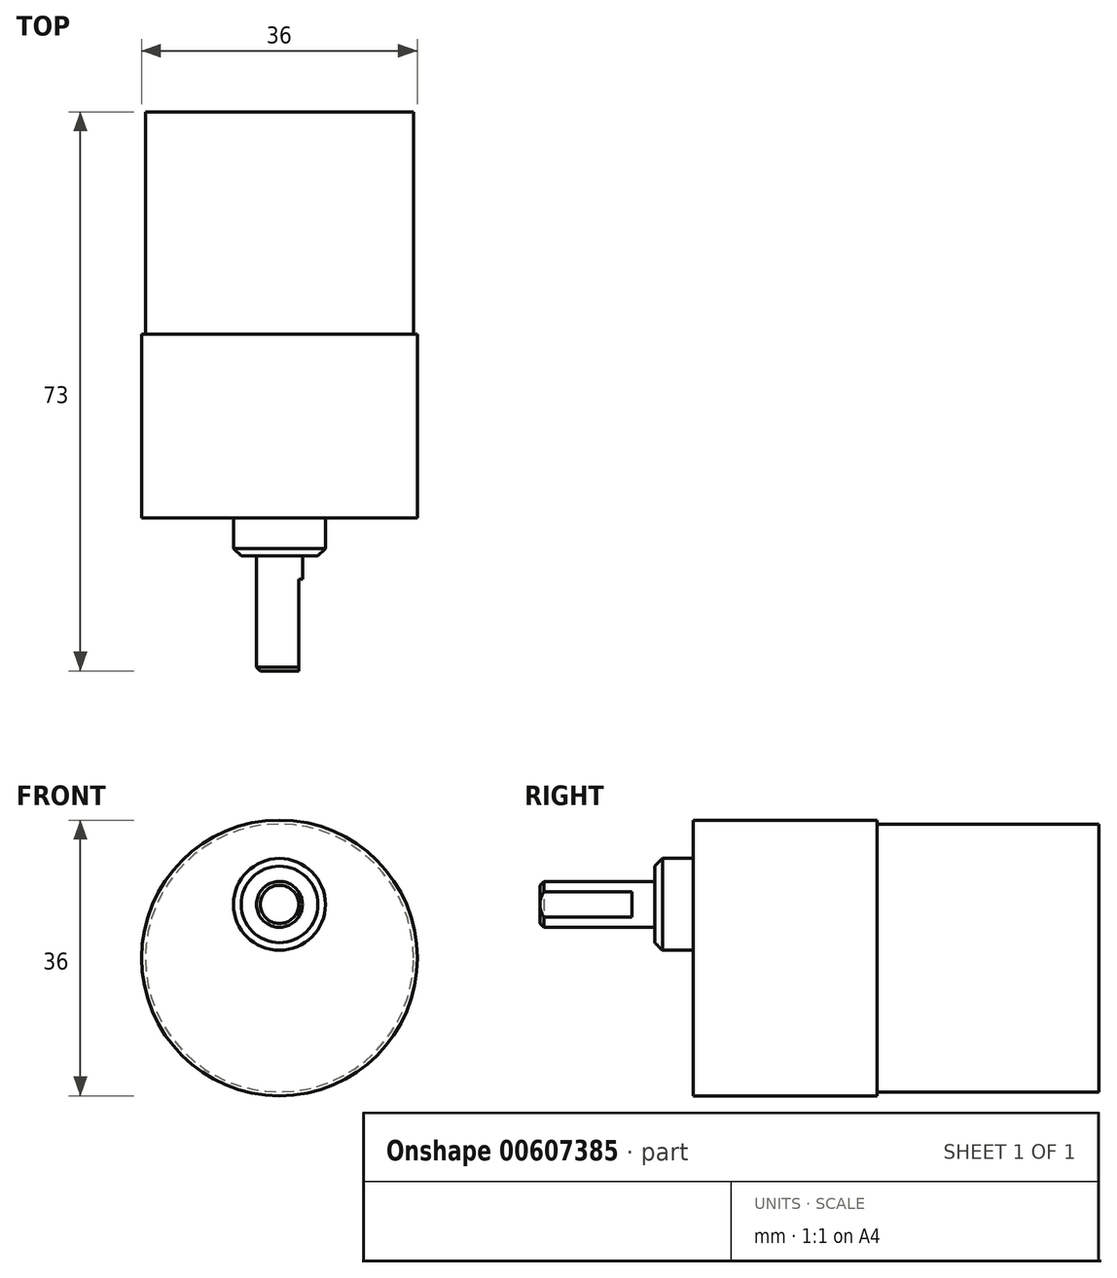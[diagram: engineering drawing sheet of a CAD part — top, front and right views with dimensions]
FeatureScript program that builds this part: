
annotation { "Feature Type Name" : "Feature", "Feature Type Description" : "" }
export const myFeature = defineFeature(function(context is Context, id is Id, definition is map)
    precondition{}
    {
        {
            var Q0;
            Q0=qCreatedBy(makeId("Front.planeOp"),FACE);
            var sketch = newSketch(context, id + "F0", { "sketchPlane" : qUnion([Q0])});
            skCircle(sketch, "E0", {"center": v(0, 0) * mm, "radius": 18 * mm});
            skCircle(sketch, "E1.cCircle", {"center": v(0, 0) * mm, "radius": 18 * mm, "construction": true});
            skLineSegment(sketch, "E1.0", {"start": v(0, -18) * mm, "end": v(-15.59, 9) * mm, "construction": true});
            skLineSegment(sketch, "E1.1", {"start": v(-15.59, 9) * mm, "end": v(15.59, 9) * mm, "construction": true});
            skLineSegment(sketch, "E1.2", {"start": v(15.59, 9) * mm, "end": v(0, -18) * mm, "construction": true});
            skSolve(sketch);
        }
        {
            var Q0;
            Q0 = qSketchRegion(id + "F0", true);
            extrude(context, id + "F1", {"entities" : qUnion([Q0]), "depth" : 24 * mm, "offsetDistance" : 25 * mm});
        }
        {
            var Q0;
            Q0=makeQuery(id+"F1.opExtrude","CAP_FACE",FACE,{"disambiguationData":[OSD([sQuery(id+"F0.wireOp",EDGE,"E0")])],"isStart":false});
            var sketch = newSketch(context, id + "F2", { "sketchPlane" : qUnion([Q0])});
            skCircle(sketch, "E2", {"center": v(0, 7) * mm, "radius": 6 * mm});
            skSolve(sketch);
        }
        {
            var Q0;
            Q0=makeQuery(id+"F2.imprint","IMPRINT",FACE,{"disambiguationData":[TD([[makeQuery(id+"F2.imprint","IMPRINT",EDGE,{"derivedFrom":sQuery(id+"F2.wireOp",EDGE,"E2")}),1.0]])]});
            extrude(context, id + "F3", {"entities" : qUnion([Q0]), "operationType" : NewBodyOperationType.ADD, "depth" : 5 * mm, "offsetDistance" : 25 * mm});
        }
        {
            var Q0;
            Q0=makeQuery(id+"F3.opExtrude","CAP_EDGE",EDGE,{"disambiguationData":[OSD([sQuery(id+"F2.wireOp",EDGE,"E2")])],"isStart":false});
            chamfer(context, id + "F4", {"entities" : qUnion([Q0]), "width" : 1 * mm, "tangentPropagation" : true});
        }
        {
            var Q0;
            Q0=makeQuery(id+"F3.opExtrude","CAP_FACE",FACE,{"disambiguationData":[OSD([sQuery(id+"F2.wireOp",EDGE,"E2")])],"isStart":false});
            var sketch = newSketch(context, id + "F5", { "sketchPlane" : qUnion([Q0])});
            skCircle(sketch, "E3", {"center": v(0, 7) * mm, "radius": 3 * mm});
            skLineSegment(sketch, "E4", {"start": v(2, 9.24) * mm, "end": v(2, 4.76) * mm, "construction": true});
            skSolve(sketch);
        }
        {
            var Q0;
            Q0=makeQuery(id+"F5.imprint","IMPRINT",FACE,{"disambiguationData":[TD([[makeQuery(id+"F5.imprint","IMPRINT",EDGE,{"derivedFrom":sQuery(id+"F5.wireOp",EDGE,"E3")}),1.0]])]});
            var Q1;
            Q1=sQuery(id+"F5.wireOp",EDGE,"E3");
            extrude(context, id + "F6", {"entities" : qUnion([Q0]), "surfaceEntities" : qUnion([Q1]), "depth" : 15 * mm, "offsetDistance" : 25 * mm});
        }
        {
            var Q0;
            Q0=makeQuery(id+"F6.opExtrude","CAP_EDGE",EDGE,{"disambiguationData":[OSD([sQuery(id+"F5.wireOp",EDGE,"E3")])],"isStart":false});
            chamfer(context, id + "F7", {"entities" : qUnion([Q0]), "width" : 0.5 * mm, "tangentPropagation" : true});
        }
        {
            var Q0;
            Q0=makeQuery(id+"F6.opExtrude","CAP_FACE",FACE,{"disambiguationData":[OSD([sQuery(id+"F5.wireOp",EDGE,"E3")])],"isStart":false});
            var sketch = newSketch(context, id + "F8", { "sketchPlane" : qUnion([Q0])});
            skLineSegment(sketch, "E5.bottom", {"start": v(4.5, 9.37) * mm, "end": v(2.5, 9.37) * mm});
            skLineSegment(sketch, "E5.top", {"start": v(4.5, 4.57) * mm, "end": v(2.5, 4.57) * mm});
            skLineSegment(sketch, "E5.left", {"start": v(4.5, 9.37) * mm, "end": v(4.5, 4.57) * mm});
            skLineSegment(sketch, "E5.right", {"start": v(2.5, 9.37) * mm, "end": v(2.5, 4.57) * mm});
            skLineSegment(sketch, "E6", {"start": v(0, 7) * mm, "end": v(4.5, 7) * mm, "construction": true});
            skSolve(sketch);
        }
        {
            var Q0;
            Q0 = qSketchRegion(id + "F8", true);
            extrude(context, id + "F9", {"entities" : qUnion([Q0]), "operationType" : NewBodyOperationType.REMOVE, "oppositeDirection" : true, "depth" : 12 * mm, "offsetDistance" : 25 * mm});
        }
        {
            var Q0;
            Q0=makeQuery(id+"F1.opExtrude","CAP_FACE",FACE,{"disambiguationData":[OSD([sQuery(id+"F0.wireOp",EDGE,"E0")])],"isStart":true});
            var sketch = newSketch(context, id + "F10", { "sketchPlane" : qUnion([Q0])});
            skCircle(sketch, "E7", {"center": v(0, 0) * mm, "radius": 17.5 * mm});
            skSolve(sketch);
        }
        {
            var Q0;
            Q0=makeQuery(id+"F10.imprint","IMPRINT",FACE,{"disambiguationData":[TD([[makeQuery(id+"F10.imprint","IMPRINT",EDGE,{"derivedFrom":sQuery(id+"F10.wireOp",EDGE,"E7")}),1.0]])]});
            extrude(context, id + "F11", {"entities" : qUnion([Q0]), "operationType" : NewBodyOperationType.ADD, "depth" : 29 * mm, "offsetDistance" : 25 * mm});
        }
    });
